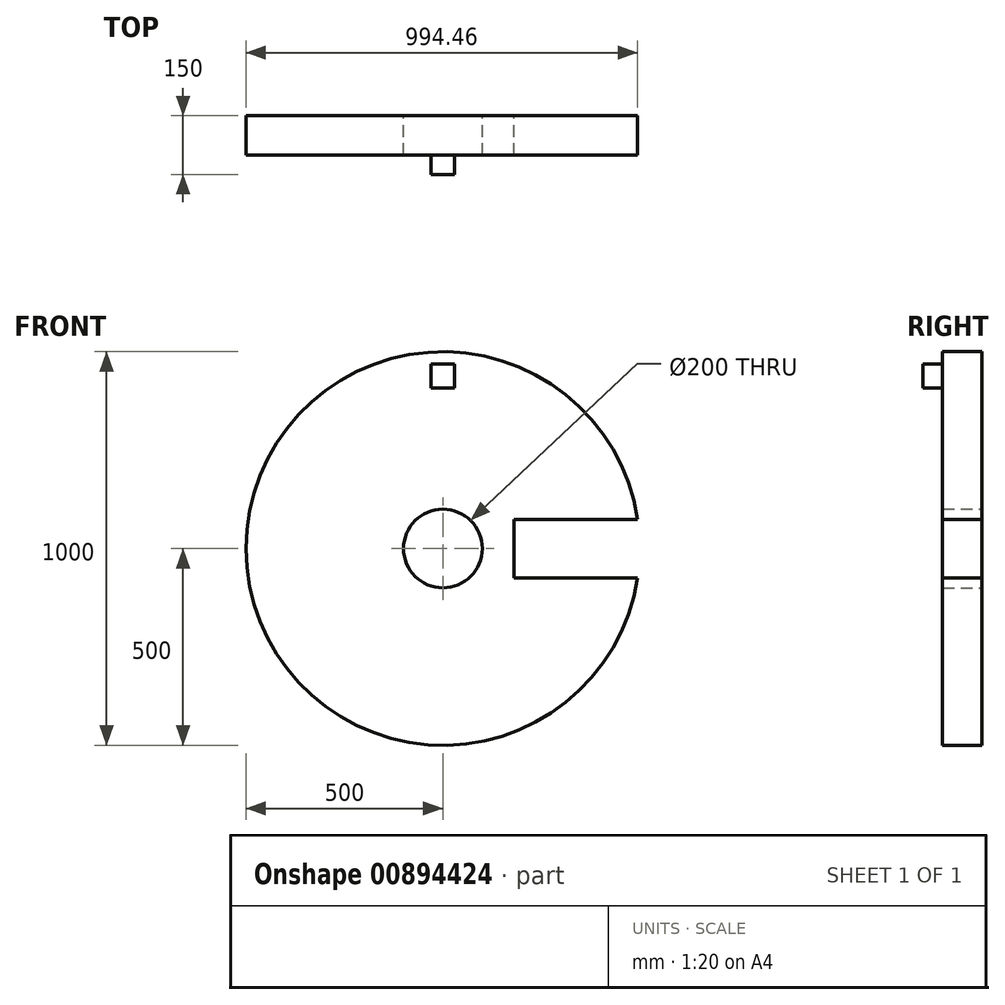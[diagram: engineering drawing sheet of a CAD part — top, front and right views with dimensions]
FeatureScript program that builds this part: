
annotation { "Feature Type Name" : "Feature", "Feature Type Description" : "" }
export const myFeature = defineFeature(function(context is Context, id is Id, definition is map)
    precondition{}
    {
        {
            var Q0;
            Q0=qCreatedBy(makeId("Front.planeOp"),FACE);
            var sketch = newSketch(context, id + "F0", { "sketchPlane" : qUnion([Q0])});
            skCircle(sketch, "E0", {"center": v(0, 0) * mm, "radius": 500 * mm});
            skLineSegment(sketch, "E1.left", {"start": v(554.92, 74.24) * mm, "end": v(554.92, -74.24) * mm});
            skLineSegment(sketch, "E2", {"start": v(0, 0) * mm, "end": v(0, -74.24) * mm});
            skLineSegment(sketch, "E3", {"start": v(0, -74.24) * mm, "end": v(0, 74.24) * mm});
            skLineSegment(sketch, "E4", {"start": v(0, -74.24) * mm, "end": v(554.92, -74.24) * mm});
            skLineSegment(sketch, "E5", {"start": v(0, 74.24) * mm, "end": v(554.92, 74.24) * mm});
            skCircle(sketch, "E6", {"center": v(0, 0) * mm, "radius": 100 * mm});
            skLineSegment(sketch, "E7", {"start": v(180.2, 74.24) * mm, "end": v(180.2, -74.24) * mm});
            skLineSegment(sketch, "E8", {"start": v(0, 0) * mm, "end": v(0, 500) * mm});
            skLineSegment(sketch, "E9.bottom", {"start": v(30, 468.36) * mm, "end": v(-30, 468.36) * mm});
            skLineSegment(sketch, "E9.top", {"start": v(30, 408.36) * mm, "end": v(-30, 408.36) * mm});
            skLineSegment(sketch, "E9.left", {"start": v(30, 468.36) * mm, "end": v(30, 408.36) * mm});
            skLineSegment(sketch, "E9.right", {"start": v(-30, 468.36) * mm, "end": v(-30, 408.36) * mm});
            skPoint(sketch, "E9.middle", {"position": v(0, 438.36) * mm});
            skSolve(sketch);
        }
        {
            var Q0;
            {var subQ1=sQuery(id+"F0.wireOp",EDGE,"E3");var subQ3=makeQuery(id+"F0.imprint","IMPRINT",VERTEX,{"derivedFrom":subQ1});Q0=makeQuery(id+"F0.imprint","IMPRINT",FACE,{"disambiguationData":[TD([[makeQuery(id+"F0.imprint","IMPRINT",EDGE,{"disambiguationData":[TD([[subQ3,1.0]])],"derivedFrom":subQ1}),1.0]])]});}
            var Q1;
            {var subQ3=sQuery(id+"F0.wireOp",EDGE,"oxylOpGK-CSzE-cepS-2aSh-l0lyYxATOx16");Q1=makeQuery(id+"F0.imprint","IMPRINT",FACE,{"disambiguationData":[TD([[makeQuery(id+"F0.imprint","IMPRINT",EDGE,{"derivedFrom":subQ3}),-1.0]])]});}
            var Q2;
            {var subQ1=sQuery(id+"F0.wireOp",EDGE,"E4");var subQ3=sQuery(id+"F0.wireOp",EDGE,"E0");var subQ4=makeQuery(id+"F0.imprint","INTERSECT",VERTEX,{"derivedFrom":[subQ3,subQ1]});Q2=makeQuery(id+"F0.imprint","IMPRINT",FACE,{"disambiguationData":[TD([[makeQuery(id+"F0.imprint","IMPRINT",EDGE,{"disambiguationData":[TD([[subQ4,1.0]])],"derivedFrom":subQ3}),1.0]])]});}
            var Q3;
            {var subQ1=sQuery(id+"F0.wireOp",EDGE,"E3");var subQ8=makeQuery(id+"F0.imprint","IMPRINT",VERTEX,{"derivedFrom":subQ1});Q3=makeQuery(id+"F0.imprint","IMPRINT",FACE,{"disambiguationData":[TD([[makeQuery(id+"F0.imprint","IMPRINT",EDGE,{"disambiguationData":[TD([[subQ8,1.0]])],"derivedFrom":subQ1}),-1.0]])]});}
            var Q4;
            {var subQ0=sQuery(id+"F0.wireOp",EDGE,"E7");Q4=makeQuery(id+"F0.imprint","IMPRINT",FACE,{"disambiguationData":[TD([[makeQuery(id+"F0.imprint","IMPRINT",EDGE,{"derivedFrom":subQ0}),-1.0]])]});}
            extrude(context, id + "F1", {"entities" : qUnion([Q0, Q1, Q2, Q3, Q4]), "depth" : 100 * mm, "offsetDistance" : 25 * mm});
        }
        {
            var Q0;
            {var subQ1=sQuery(id+"F0.wireOp",EDGE,"E3");var subQ8=makeQuery(id+"F0.imprint","IMPRINT",VERTEX,{"derivedFrom":subQ1});Q0=makeQuery(id+"F0.imprint","IMPRINT",FACE,{"disambiguationData":[TD([[makeQuery(id+"F0.imprint","IMPRINT",EDGE,{"disambiguationData":[TD([[subQ8,1.0]])],"derivedFrom":subQ1}),1.0]])]});}
            var Q1;
            {var subQ1=sQuery(id+"F0.wireOp",EDGE,"E3");var subQ8=makeQuery(id+"F0.imprint","IMPRINT",VERTEX,{"derivedFrom":subQ1});Q1=makeQuery(id+"F0.imprint","IMPRINT",FACE,{"disambiguationData":[TD([[makeQuery(id+"F0.imprint","IMPRINT",EDGE,{"disambiguationData":[TD([[subQ8,1.0]])],"derivedFrom":subQ1}),-1.0]])]});}
            extrude(context, id + "F2", {"entities" : qUnion([Q0, Q1]), "operationType" : NewBodyOperationType.ADD, "depth" : 102 * mm, "offsetDistance" : 25 * mm});
        }
        {
            var Q0;
            Q0=sQuery(id+"F0.wireOp",VERTEX,"E0.center");
            var Q1;
            Q1=makeQuery(id+"F1.opExtrude","SWEPT_BODY",BODY,{"disambiguationData":[OSD([sQuery(id+"F0.wireOp",EDGE,"E0"),sQuery(id+"F0.wireOp",EDGE,"E4"),sQuery(id+"F0.wireOp",EDGE,"E5"),sQuery(id+"F0.wireOp",EDGE,"E7")])]});
            hole(context, id + "F3", {"style" : HoleStyle.SIMPLE, "endStyle" : HoleEndStyle.THROUGH, "oppositeDirection" : true, "holeDiameter" : 200 * mm, "majorDiameter" : 5 * mm, "isTappedThrough" : true, "tappedDepth" : 12 * mm, "tapClearance" : 3, "locations" : qUnion([Q0]), "scope" : qUnion([Q1])});
        }
        {
            var Q0;
            {var subQ5=sQuery(id+"F0.wireOp",EDGE,"E9.left");Q0=makeQuery(id+"F0.imprint","IMPRINT",FACE,{"disambiguationData":[TD([[makeQuery(id+"F0.imprint","IMPRINT",EDGE,{"derivedFrom":subQ5}),1.0]])]});}
            extrude(context, id + "F4", {"entities" : qUnion([Q0]), "operationType" : NewBodyOperationType.ADD, "depth" : 100 * mm, "offsetDistance" : 25 * mm});
        }
        {
            var Q0;
            {var subQ5=sQuery(id+"F0.wireOp",EDGE,"E9.right");Q0=makeQuery(id+"F0.imprint","IMPRINT",FACE,{"disambiguationData":[TD([[makeQuery(id+"F0.imprint","IMPRINT",EDGE,{"derivedFrom":subQ5}),1.0]])]});}
            var Q1;
            {var subQ5=sQuery(id+"F0.wireOp",EDGE,"E9.left");Q1=makeQuery(id+"F0.imprint","IMPRINT",FACE,{"disambiguationData":[TD([[makeQuery(id+"F0.imprint","IMPRINT",EDGE,{"derivedFrom":subQ5}),-1.0]])]});}
            extrude(context, id + "F5", {"entities" : qUnion([Q0, Q1]), "operationType" : NewBodyOperationType.ADD, "depth" : 150 * mm, "offsetDistance" : 25 * mm});
        }
    });
